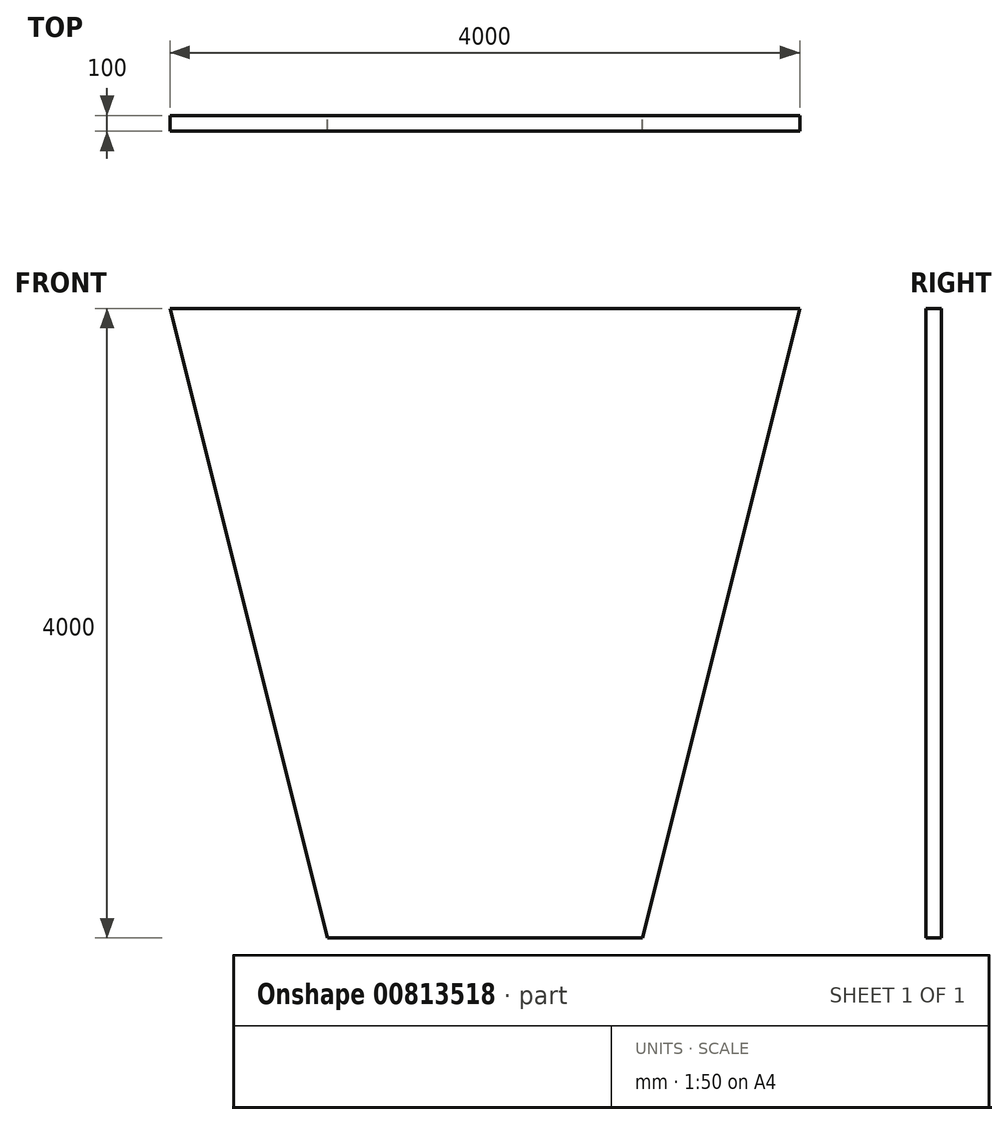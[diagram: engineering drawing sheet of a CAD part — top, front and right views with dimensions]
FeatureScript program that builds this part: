
annotation { "Feature Type Name" : "Feature", "Feature Type Description" : "" }
export const myFeature = defineFeature(function(context is Context, id is Id, definition is map)
    precondition{}
    {
        {
            var Q0;
            Q0=qCreatedBy(makeId("Front.planeOp"),FACE);
            var sketch = newSketch(context, id + "F0", { "sketchPlane" : qUnion([Q0])});
            skLineSegment(sketch, "E0", {"start": v(-2000, 0) * mm, "end": v(2000, 0) * mm});
            skLineSegment(sketch, "E1", {"start": v(0, -4000) * mm, "end": v(-1000, -4000) * mm});
            skLineSegment(sketch, "E2", {"start": v(-2000, 0) * mm, "end": v(-1000, -4000) * mm});
            skLineSegment(sketch, "E3.MirrorCS", {"start": v(2000, 0) * mm, "end": v(1000, -4000) * mm});
            skLineSegment(sketch, "E4.MirrorCS", {"start": v(0, -4000) * mm, "end": v(1000, -4000) * mm});
            skSolve(sketch);
        }
        {
            var Q0;
            Q0=makeQuery(id+"F0.imprint","IMPRINT",FACE,{"disambiguationData":[TD([[makeQuery(id+"F0.imprint","IMPRINT",EDGE,{"derivedFrom":sQuery(id+"F0.wireOp",EDGE,"E0")}),-1.0]])]});
            extrude(context, id + "F1", {"entities" : qUnion([Q0]), "depth" : 100 * mm, "offsetDistance" : 25 * mm});
        }
    });
